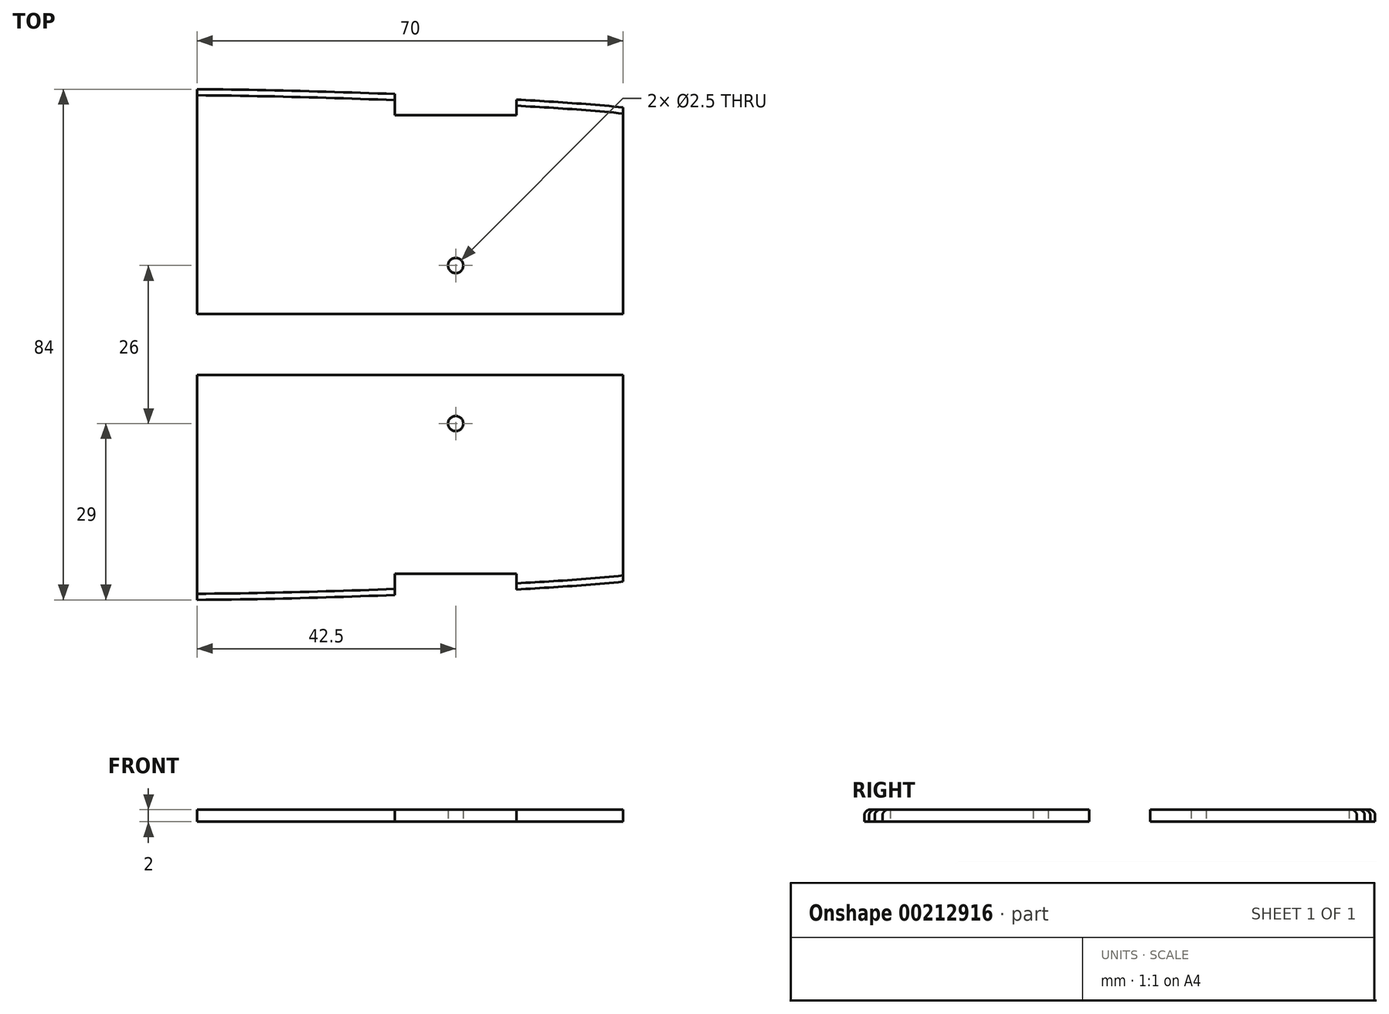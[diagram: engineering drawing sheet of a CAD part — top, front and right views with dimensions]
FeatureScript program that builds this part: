
annotation { "Feature Type Name" : "Feature", "Feature Type Description" : "" }
export const myFeature = defineFeature(function(context is Context, id is Id, definition is map)
    precondition{}
    {
        {
            var Q0;
            Q0=qCreatedBy(makeId("Top.planeOp"),FACE);
            var sketch = newSketch(context, id + "F0", { "sketchPlane" : qUnion([Q0])});
            skLineSegment(sketch, "E0.bottom", {"start": v(0, 0) * mm, "end": v(70, 0) * mm});
            skLineSegment(sketch, "E0.left", {"start": v(0, 0) * mm, "end": v(0, 37) * mm});
            skLineSegment(sketch, "E0.right", {"start": v(70, 0) * mm, "end": v(70, 34) * mm});
            skLineSegment(sketch, "E1.bottom", {"start": v(32.5, 32.7) * mm, "end": v(52.5, 32.7) * mm});
            skFitSpline(sketch, "E2", {"points": [v(0, 37) * mm, v(70, 34) * mm], "startDerivative": vector(55.75, -0.4) * mm, "endDerivative": vector(48.5, -5) * mm});
            skLineSegment(sketch, "E3", {"start": v(32.5, 32.7) * mm, "end": v(32.5, 36.2) * mm});
            skLineSegment(sketch, "E4", {"start": v(52.5, 32.7) * mm, "end": v(52.5, 35.29) * mm});
            skLineSegment(sketch, "E5", {"start": v(42.5, 32.7) * mm, "end": v(42.5, 0) * mm, "construction": true});
            skCircle(sketch, "E6", {"center": v(42.5, 8) * mm, "radius": 1.25 * mm});
            skSolve(sketch);
        }
        {
            var Q0;
            Q0=makeQuery(id+"F0.imprint","IMPRINT",FACE,{"disambiguationData":[TD([[makeQuery(id+"F0.imprint","IMPRINT",EDGE,{"derivedFrom":sQuery(id+"F0.wireOp",EDGE,"E0.left")}),-1.0]])]});
            extrude(context, id + "F1", {"entities" : qUnion([Q0]), "depth" : 2 * mm});
        }
        {
            var Q0;
            Q0=makeQuery(id+"F0.imprint","IMPRINT",FACE,{"disambiguationData":[TD([[makeQuery(id+"F0.imprint","IMPRINT",EDGE,{"derivedFrom":sQuery(id+"F0.wireOp",EDGE,"E0.bottom")}),1.0]])]});
            extrude(context, id + "F2", {"entities" : qUnion([Q0]), "operationType" : NewBodyOperationType.ADD, "depth" : 2 * mm});
        }
        {
            var Q0;
            Q0=makeQuery(id+"F1.opExtrude","CAP_EDGE",EDGE,{"disambiguationData":[OSD([sQuery(id+"F0.wireOp",EDGE,"E2")])],"isStart":false});
            var Q1;
            Q1=makeQuery(id+"F1.opExtrude","CAP_EDGE",EDGE,{"disambiguationData":[OSD([sQuery(id+"F0.wireOp",EDGE,"E2")])],"isStart":false});
            var Q2;
            Q2=makeQuery(id+"F2.opExtrude","CAP_EDGE",EDGE,{"disambiguationData":[OSD([sQuery(id+"F0.wireOp",EDGE,"is763EvT-fs9t-QccU-FjVb-8aT8NWx21cw3.top")])],"isStart":false});
            var Q3;
            Q3=makeQuery(id+"F2.opExtrude","CAP_EDGE",EDGE,{"disambiguationData":[OSD([sQuery(id+"F0.wireOp",EDGE,"E0.bottom")])],"isStart":false});
            fillet(context, id + "F3", {"entities" : qUnion([Q0, Q1, Q2, Q3]), "radius" : 1 * mm, "tangentPropagation" : true, "allowEdgeOverflow" : false});
        }
        {
            var Q0;
            Q0=makeQuery(id+"F1.opExtrude","SWEPT_FACE",FACE,{"disambiguationData":[OSD([sQuery(id+"F0.wireOp",EDGE,"E0.bottom")])]});
            cPlane(context, id + "F4", {"entities" : qUnion([Q0]), "cplaneType" : CPlaneType.OFFSET, "offset" : 5 * mm, "width" : 150 * mm, "height" : 150 * mm});
        }
        {
            var Q0;
            Q0=makeQuery(id+"F1.opExtrude","SWEPT_BODY",BODY,{"disambiguationData":[OSD([sQuery(id+"F0.wireOp",EDGE,"E0.left"),sQuery(id+"F0.wireOp",EDGE,"E0.right"),sQuery(id+"F0.wireOp",EDGE,"E1.bottom"),sQuery(id+"F0.wireOp",EDGE,"E2"),sQuery(id+"F0.wireOp",EDGE,"E3"),sQuery(id+"F0.wireOp",EDGE,"E4"),sQuery(id+"F0.wireOp",EDGE,"E2"),sQuery(id+"F0.wireOp",EDGE,"E0.bottom"),sQuery(id+"F0.wireOp",EDGE,"E6")])]});
            var Q1;
            Q1=qCreatedBy(id+"F4.planeOp",FACE);
            mirror(context, id + "F5", {"entities" : qUnion([Q0]), "mirrorPlane" : qUnion([Q1])});
        }
    });
